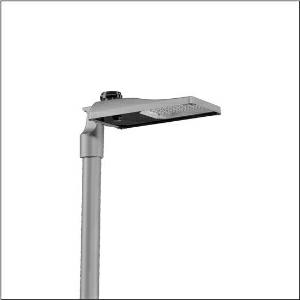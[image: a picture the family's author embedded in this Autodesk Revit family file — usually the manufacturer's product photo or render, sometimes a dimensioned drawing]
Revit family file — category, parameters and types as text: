
# Revit family: streetlight_sl_31_mini___st1_0a_5xh2d3bm08ja_c740
name_source: partatom
category: Lighting Fixtures
units: mm (PartAtom-declared; Revit-internal decimal feet)

## family parameters
Cut with Voids When Loaded = No
Host = Face
Light Source = No
Part Type = Normal
Room Calculation Point = No
Round Connector Dimension = Use Diameter
Shared = No

## types (1)
- --- (1 x LED, 12270 lm, 82.5 W, 3000K)
    Apparent Load = 83 VA
    CIE Flux Codes = 40 73 97 100 100
    Color Rendering = 70
    Color Temperature = 3000K
    Default Elevation = 1800 mm
    Description = Streetlight SL 31 mini NEMA (7pin) mast luminaire for post-top, side-entry; light control with lens of PMMA; light distribution: ST1.0a, direct asymmetric distribution, for standard-compliant lighting for roads and squares; LED: luminous flux: 12.270lm, light colour: 730, colour temperature: 3000K; luminous efficacy: 148,7lm/W; control: pre-setting: linear dimming characteristic, flexible luminous flux parameterisation, time-dependent luminous flux control, constant luminous flux control, intelligent temperature release in ECG and LED module, overheat protection; luminaire housing, of diecast aluminium, SITECO metallic grey (DB 702S), corrosivity category C5 high according to DIN EN ISO 12944; cover of toughened safety glass, transparent, mast flange of diecast aluminium, SITECO metallic grey (DB 702S), spigot size: 76/60mm, mast flange included unmounted; cable length: 10,5m, connection cable pre-assembled; mains connection: 220..240V, AC, 50/60Hz; power consumption (at start of service life): 82,5W / (at end of service life): 90,1W / (with reduced operation 50%): 36,8W; protection rating (complete): IP66; insulation class (complete): insulation class I (protective earthing); impact resistance: IK09; certification: CE, ENEC, ENEC+, VDE, UKCA; permissible operating ambient temperature for outdoor applications: -40..+50°C; packaging unit: 1 piece

Light Distribution: ST1.0a
    Height = 76 mm
    Lamp = 1 x LED
    Lamp Light Flux = 12270 lm
    Lamp Power = 82.5 W
    Lamp count = 1
    Length = 547 mm
    Luminous efficacy = 149 lm/W
    Manufacturer = Siteco
    ModVariant = No
    Model = 5XH2D3BM08JA
    Number of Poles = 1
    OnlyDefault = Yes
    Power Factor = 1
    Product Name = Streetlight SL 31 mini | ST1.0a
    Product group = mast luminaire | pylon top
    ProductGroupID = 6100
    Protection Class = Protection class I
    Protection Degree = IP 66
    RLX_Detail_Level = 1
    RLX_Emergency_Light_Flux = 0 lm
    RLX_Emergency_Type = 0
    RLX_Emergency_Type_DB = No
    RlxData = <blob elided: 40229 chars, md5=08a50c39>
    Socket = socket
    Standby Power = 0 W
    System Light Flux = 12270 lm
    System Power = 83 W
    Type Comments = factory setting: luminous flux: 100 % | dim-lin: 254 | 870 mA
    Type Image = l_1300324.jpg
    URL = http://relux.com
    VarID = @adj_057435
    Voltage = 0 V
    Weight = 0.00 kg
    Width = 265 mm

## geometry (parser evidence)
native form markers: Blend x4, Sweep x11
no freeform markers — native parametric forms only
